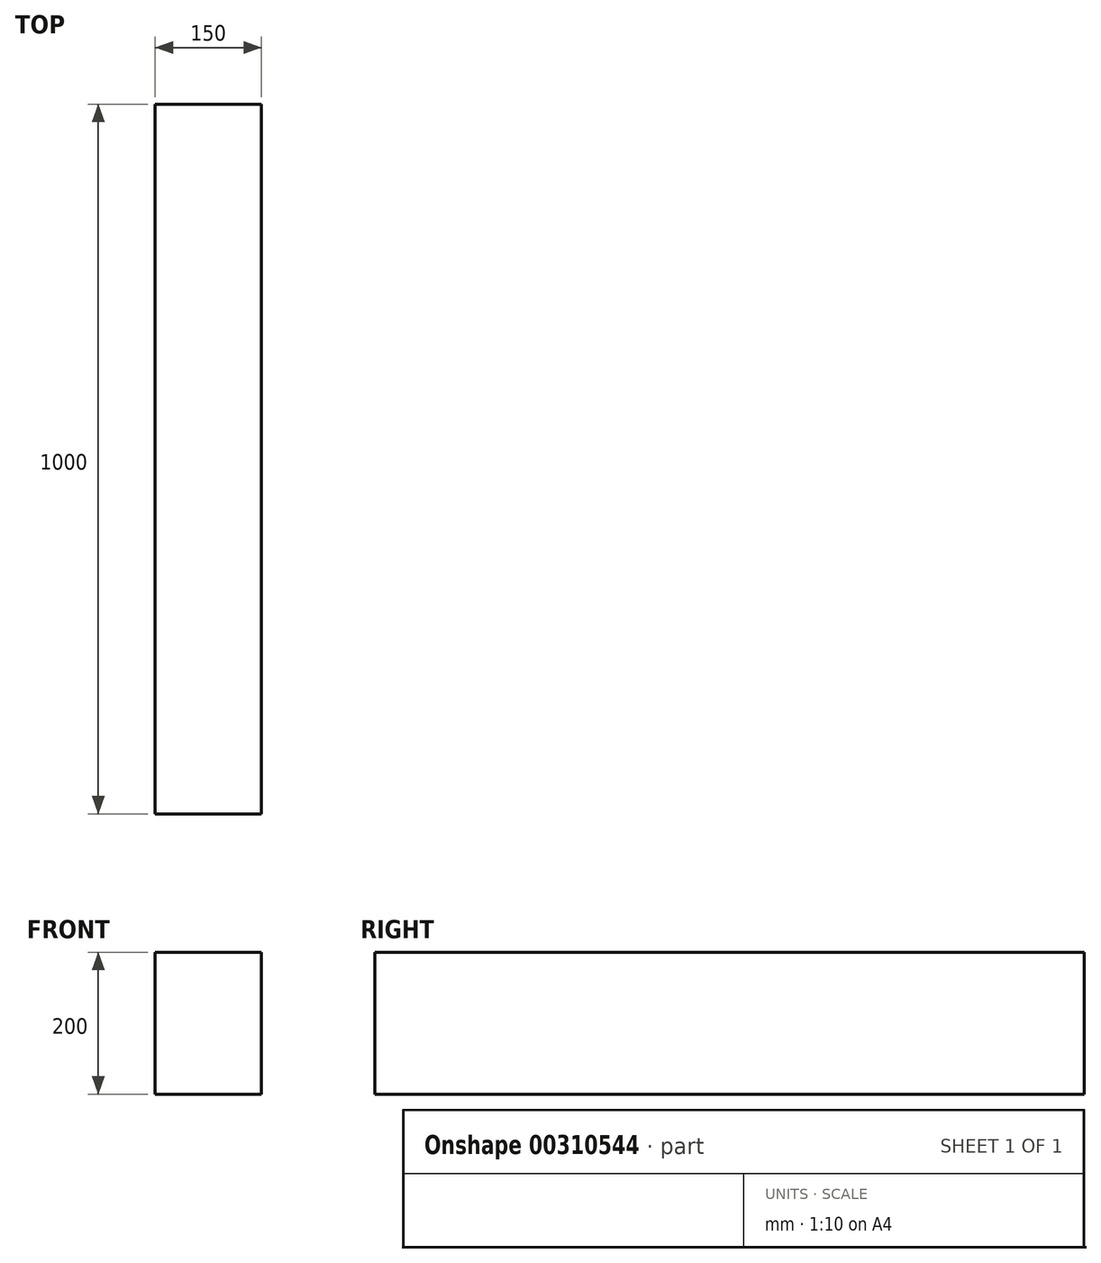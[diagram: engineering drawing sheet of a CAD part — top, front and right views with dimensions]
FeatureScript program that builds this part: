
annotation { "Feature Type Name" : "Feature", "Feature Type Description" : "" }
export const myFeature = defineFeature(function(context is Context, id is Id, definition is map)
    precondition{}
    {
        {
            var Q0;
            Q0=qCreatedBy(makeId("Right.planeOp"),FACE);
            var sketch = newSketch(context, id + "F0", { "sketchPlane" : qUnion([Q0])});
            skLineSegment(sketch, "E0.bottom", {"start": v(0, 0) * mm, "end": v(-1000, 0) * mm});
            skLineSegment(sketch, "E0.top", {"start": v(0, -200) * mm, "end": v(-1000, -200) * mm});
            skLineSegment(sketch, "E0.left", {"start": v(0, 0) * mm, "end": v(0, -200) * mm});
            skLineSegment(sketch, "E0.right", {"start": v(-1000, 0) * mm, "end": v(-1000, -200) * mm});
            skSolve(sketch);
        }
        {
            var Q0;
            Q0=makeQuery(id+"F0.imprint","IMPRINT",FACE,{"disambiguationData":[TD([[makeQuery(id+"F0.imprint","IMPRINT",EDGE,{"derivedFrom":sQuery(id+"F0.wireOp",EDGE,"E0.bottom")}),1.0]])]});
            extrude(context, id + "F1", {"entities" : qUnion([Q0]), "depth" : 150 * mm});
        }
    });
